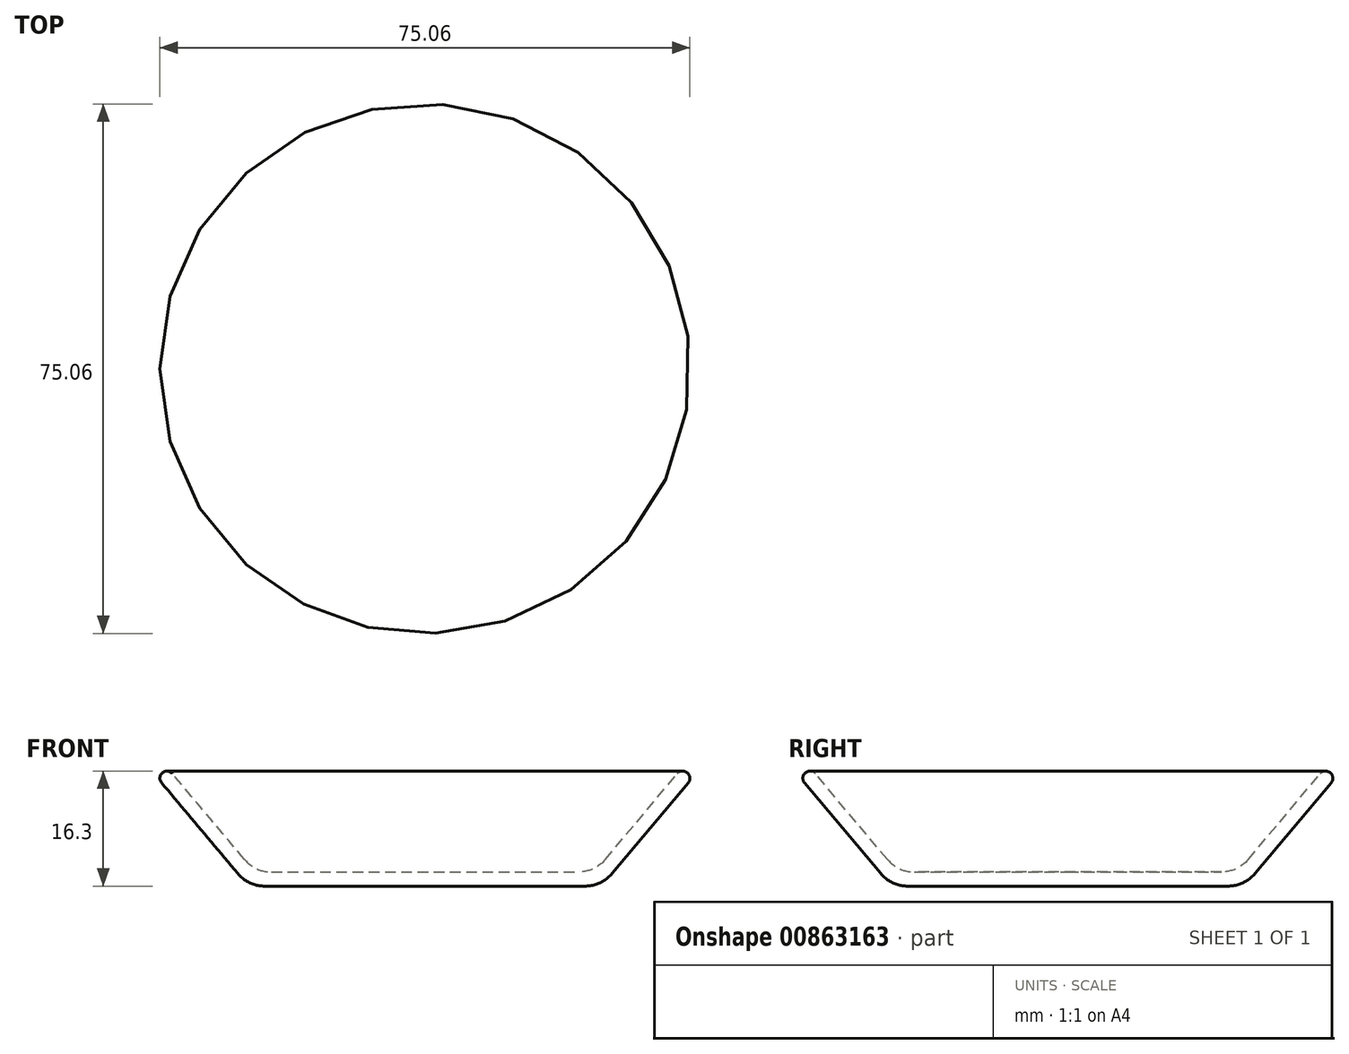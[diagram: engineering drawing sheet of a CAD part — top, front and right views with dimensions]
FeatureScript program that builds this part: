
annotation { "Feature Type Name" : "Feature", "Feature Type Description" : "" }
export const myFeature = defineFeature(function(context is Context, id is Id, definition is map)
    precondition{}
    {
        {
            var Q0;
            Q0=qCreatedBy(makeId("Front.planeOp"),FACE);
            var sketch = newSketch(context, id + "F0", { "sketchPlane" : qUnion([Q0])});
            skLineSegment(sketch, "E0", {"start": v(0, 0) * mm, "end": v(21.74, 0) * mm});
            skLineSegment(sketch, "E1", {"start": v(25.57, 1.79) * mm, "end": v(35.76, 13.94) * mm});
            skLineSegment(sketch, "E2.0", {"start": v(26.5, -0.21) * mm, "end": v(37.3, 12.65) * mm});
            skLineSegment(sketch, "E2.1", {"start": v(0, -2) * mm, "end": v(22.67, -2) * mm});
            skLineSegment(sketch, "E3", {"start": v(37.27, 13.97) * mm, "end": v(37.27, 13.97) * mm});
            skLineSegment(sketch, "E4", {"start": v(0, -2) * mm, "end": v(0, 47.87) * mm});
            skPoint(sketch, "E5.visualSharp", {"position": v(24.07, 0) * mm});
            skArc(sketch, "E5.filletArc", {"start": v(21.74, 0) * mm, "mid": v(23.85, 0.47) * mm, "end": v(25.57, 1.79) * mm});
            skPoint(sketch, "E6.visualSharp", {"position": v(25, -2) * mm});
            skArc(sketch, "E6.filletArc", {"start": v(22.67, -2) * mm, "mid": v(24.78, -1.53) * mm, "end": v(26.5, -0.21) * mm});
            skPoint(sketch, "E7.visualSharp", {"position": v(37.86, 13.32) * mm});
            skArc(sketch, "E7.filletArc", {"start": v(37.3, 12.65) * mm, "mid": v(37.53, 13.32) * mm, "end": v(37.27, 13.97) * mm});
            skPoint(sketch, "E8.visualSharp", {"position": v(36.5, 14.82) * mm});
            skArc(sketch, "E8.filletArc", {"start": v(37.27, 13.97) * mm, "mid": v(36.51, 14.3) * mm, "end": v(35.76, 13.94) * mm});
            skSolve(sketch);
        }
        {
            var Q0;
            Q0 = qSketchRegion(id + "F0", true);
            var Q1;
            Q1=sQuery(id+"F0.wireOp",EDGE,"E4");
            revolve(context, id + "F1", {"surfaceOperationType" : NewSurfaceOperationType.NEW, "entities" : qUnion([Q0]), "axis" : qUnion([Q1]), "revolveType" : RevolveType.FULL});
        }
    });
